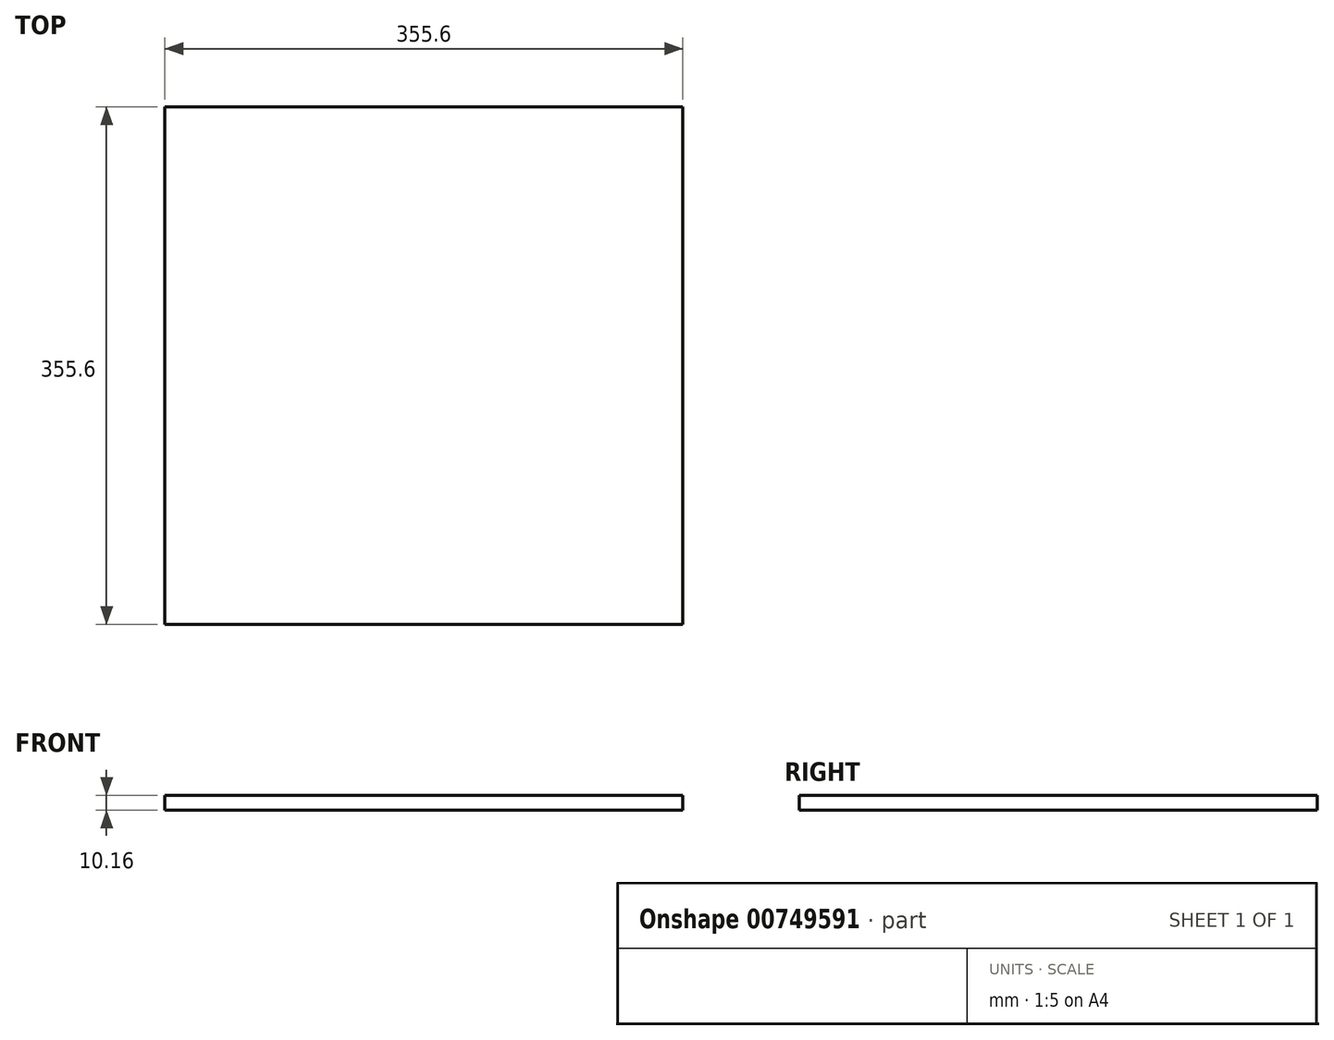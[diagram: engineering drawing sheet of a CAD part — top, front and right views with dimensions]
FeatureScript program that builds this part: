
annotation { "Feature Type Name" : "Feature", "Feature Type Description" : "" }
export const myFeature = defineFeature(function(context is Context, id is Id, definition is map)
    precondition{}
    {
        {
            var Q0;
            Q0=qCreatedBy(makeId("Top.planeOp"),FACE);
            var sketch = newSketch(context, id + "F0", { "sketchPlane" : qUnion([Q0])});
            skLineSegment(sketch, "E0.bottom", {"start": v(-152.37, 224.34) * mm, "end": v(203.23, 224.34) * mm});
            skLineSegment(sketch, "E0.top", {"start": v(-152.37, -131.26) * mm, "end": v(203.23, -131.26) * mm});
            skLineSegment(sketch, "E0.left", {"start": v(-152.37, 224.34) * mm, "end": v(-152.37, -131.26) * mm});
            skLineSegment(sketch, "E0.right", {"start": v(203.23, 224.34) * mm, "end": v(203.23, -131.26) * mm});
            skSolve(sketch);
        }
        {
            var Q0;
            Q0 = qSketchRegion(id + "F0", true);
            extrude(context, id + "F1", {"entities" : qUnion([Q0]), "depth" : 10.16 * mm, "offsetDistance" : 25.4 * mm});
        }
    });
